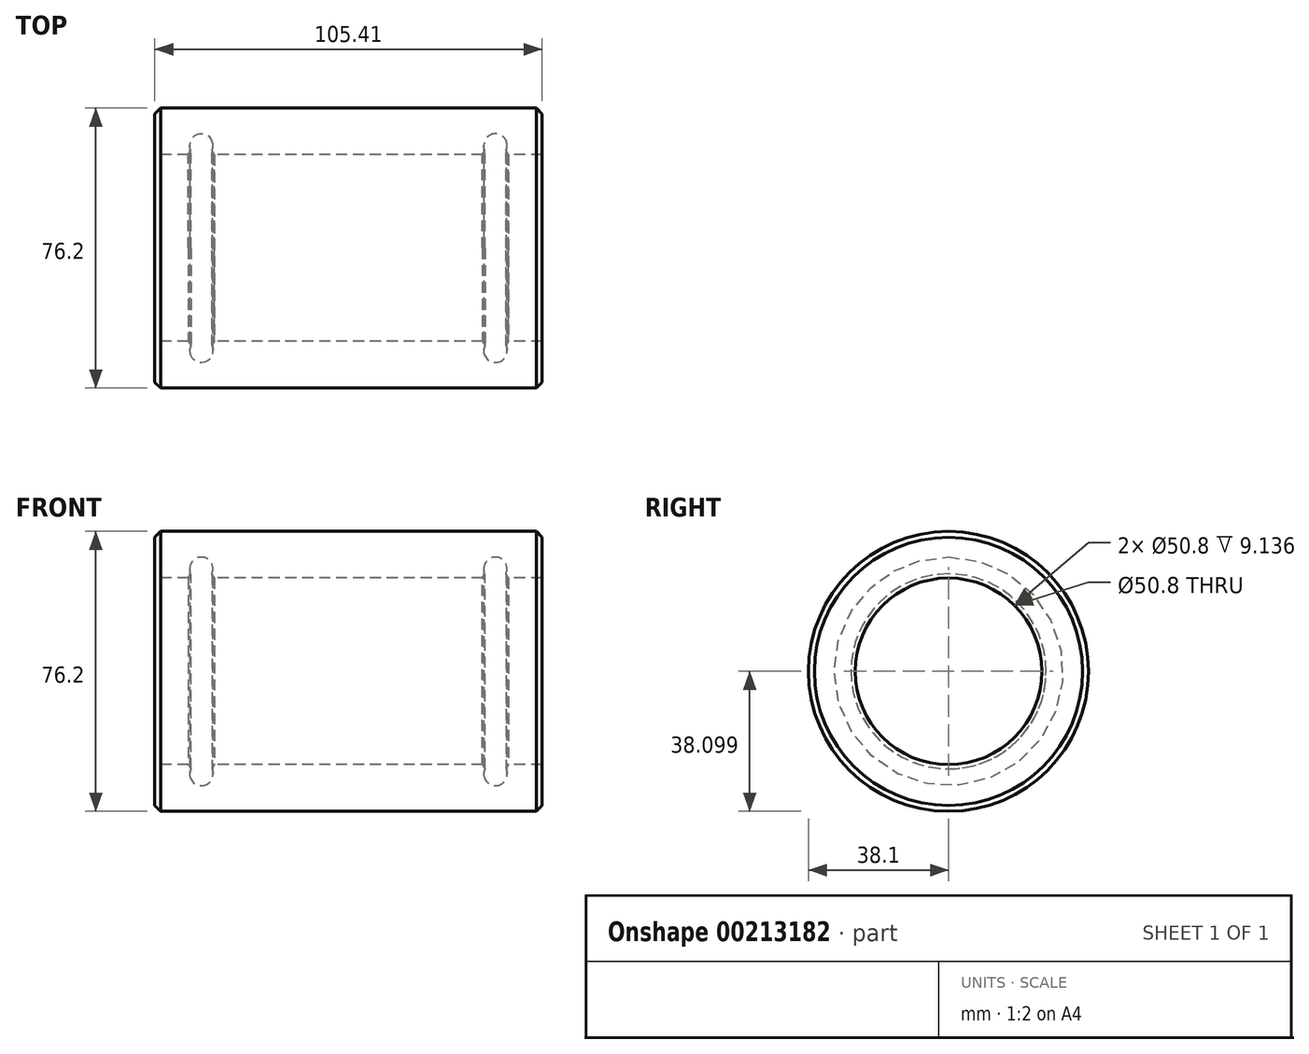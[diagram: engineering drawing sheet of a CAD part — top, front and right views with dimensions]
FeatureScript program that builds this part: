
annotation { "Feature Type Name" : "Feature", "Feature Type Description" : "" }
export const myFeature = defineFeature(function(context is Context, id is Id, definition is map)
    precondition{}
    {
        {
            var Q0;
            Q0=qCreatedBy(makeId("Front.planeOp"),FACE);
            var sketch = newSketch(context, id + "F0", { "sketchPlane" : qUnion([Q0])});
            skLineSegment(sketch, "E0", {"start": v(-105.4, 38.1) * mm, "end": v(0.02, 38.1) * mm});
            skLineSegment(sketch, "E1", {"start": v(0.02, 38.1) * mm, "end": v(0.02, 25.4) * mm});
            skLineSegment(sketch, "E2", {"start": v(0.02, 25.4) * mm, "end": v(-10.78, 25.4) * mm});
            skLineSegment(sketch, "E3", {"start": v(-105.4, 38.1) * mm, "end": v(-105.4, 25.4) * mm});
            skLineSegment(sketch, "E4", {"start": v(-105.4, 25.4) * mm, "end": v(-94.6, 25.4) * mm});
            skArc(sketch, "E5", {"start": v(-90.79, 25.4) * mm, "mid": v(-92.7, 31.11) * mm, "end": v(-94.6, 25.4) * mm});
            skArc(sketch, "E6", {"start": v(-10.78, 25.4) * mm, "mid": v(-12.68, 31.11) * mm, "end": v(-14.59, 25.4) * mm});
            skLineSegment(sketch, "E7", {"start": v(-90.79, 25.4) * mm, "end": v(-14.59, 25.4) * mm});
            skLineSegment(sketch, "E8", {"start": v(-105.41, 0) * mm, "end": v(0, 0) * mm, "construction": true});
            skLineSegment(sketch, "E9", {"start": v(-105.41, 0) * mm, "end": v(-105.41, 4.05) * mm});
            skLineSegment(sketch, "E10", {"start": v(0, 0) * mm, "end": v(0, 1.09) * mm});
            skSolve(sketch);
        }
        {
            var Q0;
            Q0=makeQuery(id+"F0.imprint","IMPRINT",FACE,{"disambiguationData":[TD([[makeQuery(id+"F0.imprint","IMPRINT",EDGE,{"derivedFrom":sQuery(id+"F0.wireOp",EDGE,"E0")}),-1.0]])]});
            var Q1;
            Q1=sQuery(id+"F0.wireOp",EDGE,"E8");
            revolve(context, id + "F1", {"entities" : qUnion([Q0]), "axis" : qUnion([Q1]), "revolveType" : RevolveType.FULL});
        }
        {
            var Q0;
            Q0=makeQuery(id+"F1.opRevolve","SWEPT_EDGE",EDGE,{"disambiguationData":[OSD([sQuery(id+"F0.wireOp",EDGE,"E0"),sQuery(id+"F0.wireOp",EDGE,"E3")])]});
            var Q1;
            Q1=makeQuery(id+"F1.opRevolve","SWEPT_EDGE",EDGE,{"disambiguationData":[OSD([sQuery(id+"F0.wireOp",EDGE,"E0"),sQuery(id+"F0.wireOp",EDGE,"E1")])]});
            chamfer(context, id + "F2", {"entities" : qUnion([Q0, Q1]), "width" : 1.6 * mm, "tangentPropagation" : true});
        }
        {
            var Q0;
            Q0=makeQuery(id+"F1.opRevolve","SWEPT_EDGE",EDGE,{"disambiguationData":[OSD([sQuery(id+"F0.wireOp",EDGE,"E2"),sQuery(id+"F0.wireOp",EDGE,"E6")])]});
            var Q1;
            Q1=makeQuery(id+"F1.opRevolve","SWEPT_EDGE",EDGE,{"disambiguationData":[OSD([sQuery(id+"F0.wireOp",EDGE,"E6"),sQuery(id+"F0.wireOp",EDGE,"E7")])]});
            var Q2;
            Q2=makeQuery(id+"F1.opRevolve","SWEPT_EDGE",EDGE,{"disambiguationData":[OSD([sQuery(id+"F0.wireOp",EDGE,"E5"),sQuery(id+"F0.wireOp",EDGE,"E7")])]});
            var Q3;
            Q3=makeQuery(id+"F1.opRevolve","SWEPT_EDGE",EDGE,{"disambiguationData":[OSD([sQuery(id+"F0.wireOp",EDGE,"E4"),sQuery(id+"F0.wireOp",EDGE,"E5")])]});
            chamfer(context, id + "F3", {"entities" : qUnion([Q0, Q1, Q2, Q3]), "width" : 0.8 * mm, "tangentPropagation" : true});
        }
    });
